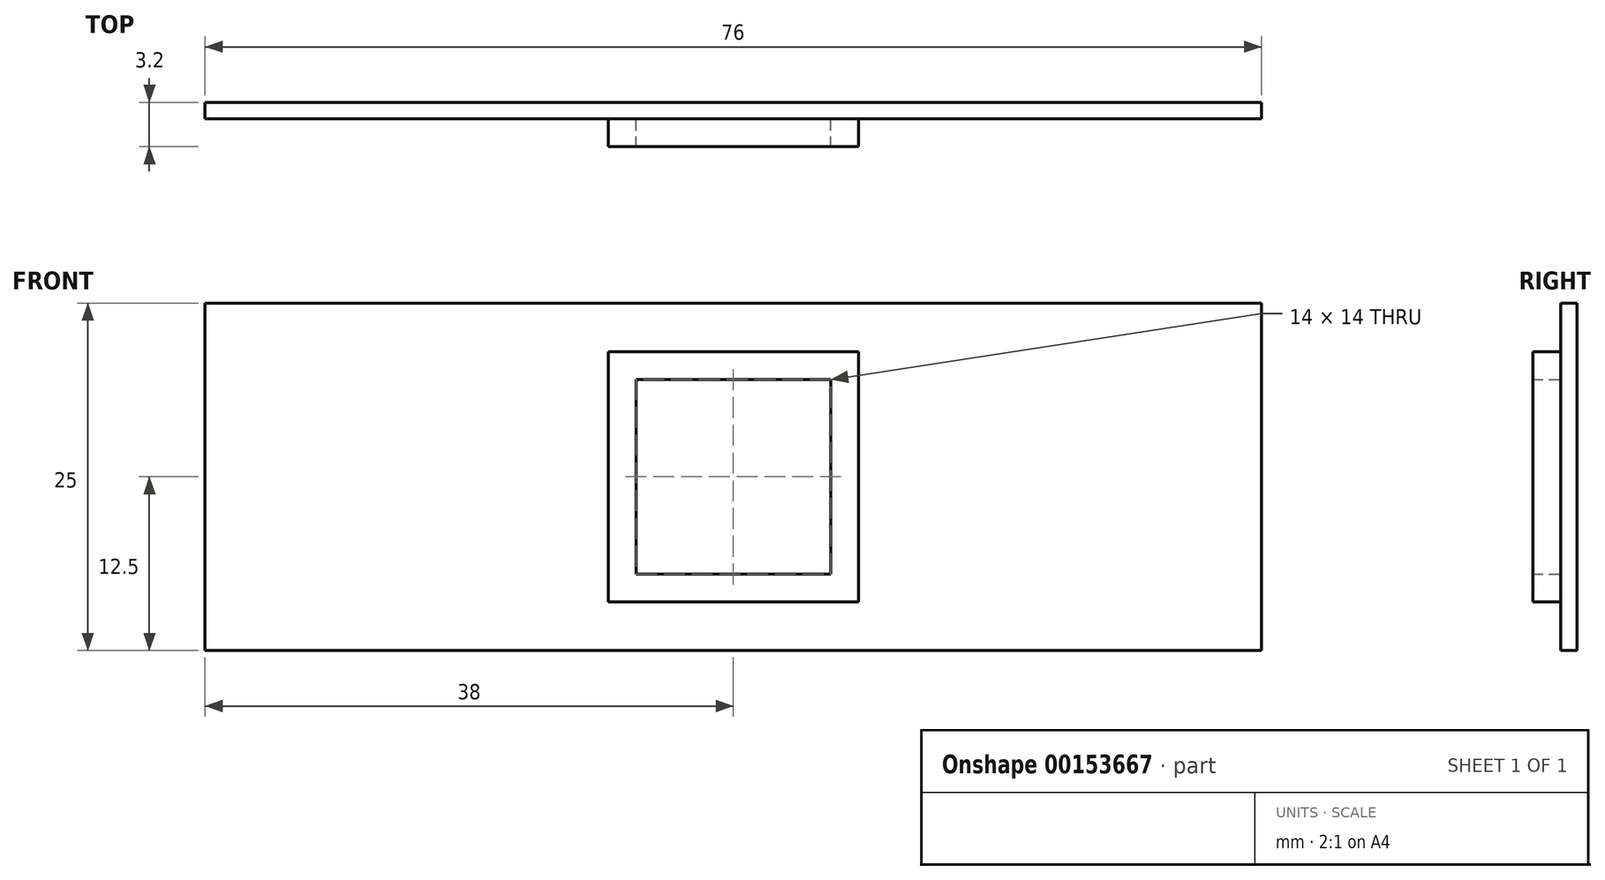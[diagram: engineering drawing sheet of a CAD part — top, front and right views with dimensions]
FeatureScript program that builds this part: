
annotation { "Feature Type Name" : "Feature", "Feature Type Description" : "" }
export const myFeature = defineFeature(function(context is Context, id is Id, definition is map)
    precondition{}
    {
        {
            var Q0;
            Q0=qCreatedBy(makeId("Front.planeOp"),FACE);
            var sketch = newSketch(context, id + "F0", { "sketchPlane" : qUnion([Q0])});
            skLineSegment(sketch, "E0.bottom", {"start": v(9, 9) * mm, "end": v(-9, 9) * mm});
            skLineSegment(sketch, "E0.top", {"start": v(9, -9) * mm, "end": v(-9, -9) * mm});
            skLineSegment(sketch, "E0.left", {"start": v(9, 9) * mm, "end": v(9, -9) * mm});
            skLineSegment(sketch, "E0.right", {"start": v(-9, 9) * mm, "end": v(-9, -9) * mm});
            skPoint(sketch, "E0.middle", {"position": v(0, 0) * mm});
            skLineSegment(sketch, "E1.bottom", {"start": v(7, 7) * mm, "end": v(-7, 7) * mm});
            skLineSegment(sketch, "E1.top", {"start": v(7, -7) * mm, "end": v(-7, -7) * mm});
            skLineSegment(sketch, "E1.left", {"start": v(7, 7) * mm, "end": v(7, -7) * mm});
            skLineSegment(sketch, "E1.right", {"start": v(-7, 7) * mm, "end": v(-7, -7) * mm});
            skSolve(sketch);
        }
        {
            var Q0;
            Q0=makeQuery(id+"F0.imprint","IMPRINT",FACE,{"disambiguationData":[TD([[makeQuery(id+"F0.imprint","IMPRINT",EDGE,{"derivedFrom":sQuery(id+"F0.wireOp",EDGE,"E0.bottom")}),1.0]])]});
            extrude(context, id + "F1", {"entities" : qUnion([Q0]), "depth" : 2 * mm});
        }
        {
            var Q0;
            Q0=qCreatedBy(makeId("Front.planeOp"),FACE);
            var sketch = newSketch(context, id + "F2", { "sketchPlane" : qUnion([Q0])});
            skLineSegment(sketch, "E2.bottom", {"start": v(-38, 12.5) * mm, "end": v(38, 12.5) * mm});
            skLineSegment(sketch, "E2.top", {"start": v(-38, -12.5) * mm, "end": v(38, -12.5) * mm});
            skLineSegment(sketch, "E2.left", {"start": v(-38, 12.5) * mm, "end": v(-38, -12.5) * mm});
            skLineSegment(sketch, "E2.right", {"start": v(38, 12.5) * mm, "end": v(38, -12.5) * mm});
            skPoint(sketch, "E2.middle", {"position": v(0, 0) * mm});
            skSolve(sketch);
        }
        {
            var Q0;
            Q0=makeQuery(id+"F2.imprint","IMPRINT",FACE,{"disambiguationData":[TD([[makeQuery(id+"F2.imprint","IMPRINT",EDGE,{"derivedFrom":sQuery(id+"F2.wireOp",EDGE,"E2.bottom")}),-1.0]])]});
            extrude(context, id + "F3", {"entities" : qUnion([Q0]), "oppositeDirection" : true, "depth" : 1.2 * mm});
        }
    });
